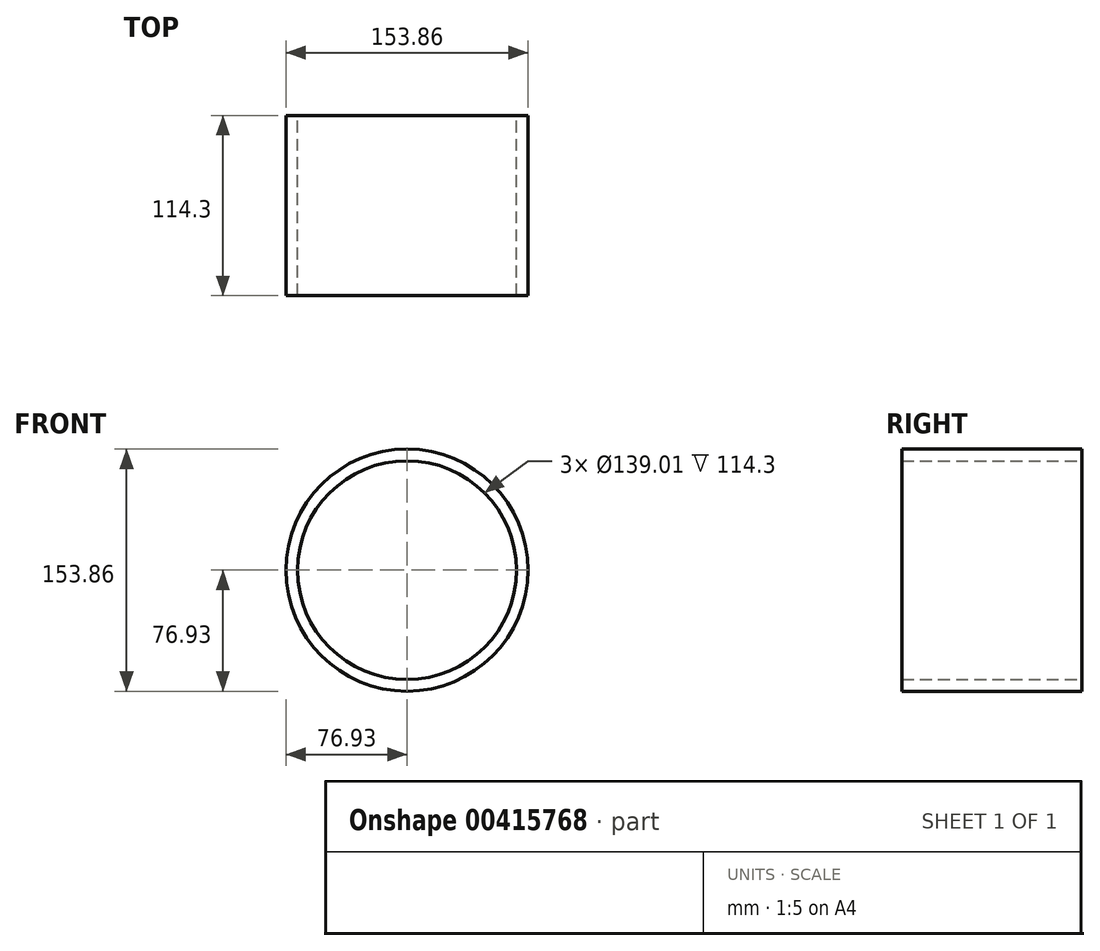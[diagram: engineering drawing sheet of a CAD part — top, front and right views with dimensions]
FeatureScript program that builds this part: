
annotation { "Feature Type Name" : "Feature", "Feature Type Description" : "" }
export const myFeature = defineFeature(function(context is Context, id is Id, definition is map)
    precondition{}
    {
        {
            var Q0;
            Q0=qCreatedBy(makeId("Front.planeOp"),FACE);
            var sketch = newSketch(context, id + "F0", { "sketchPlane" : qUnion([Q0])});
            skCircle(sketch, "E0", {"center": v(0, 0) * mm, "radius": 76.93 * mm});
            skCircle(sketch, "E1", {"center": v(0, 0) * mm, "radius": 69.5 * mm});
            skSolve(sketch);
        }
        {
            var Q0;
            Q0 = qSketchRegion(id + "F0", true);
            extrude(context, id + "F1", {"entities" : qUnion([Q0]), "depth" : 114.3 * mm});
        }
    });
